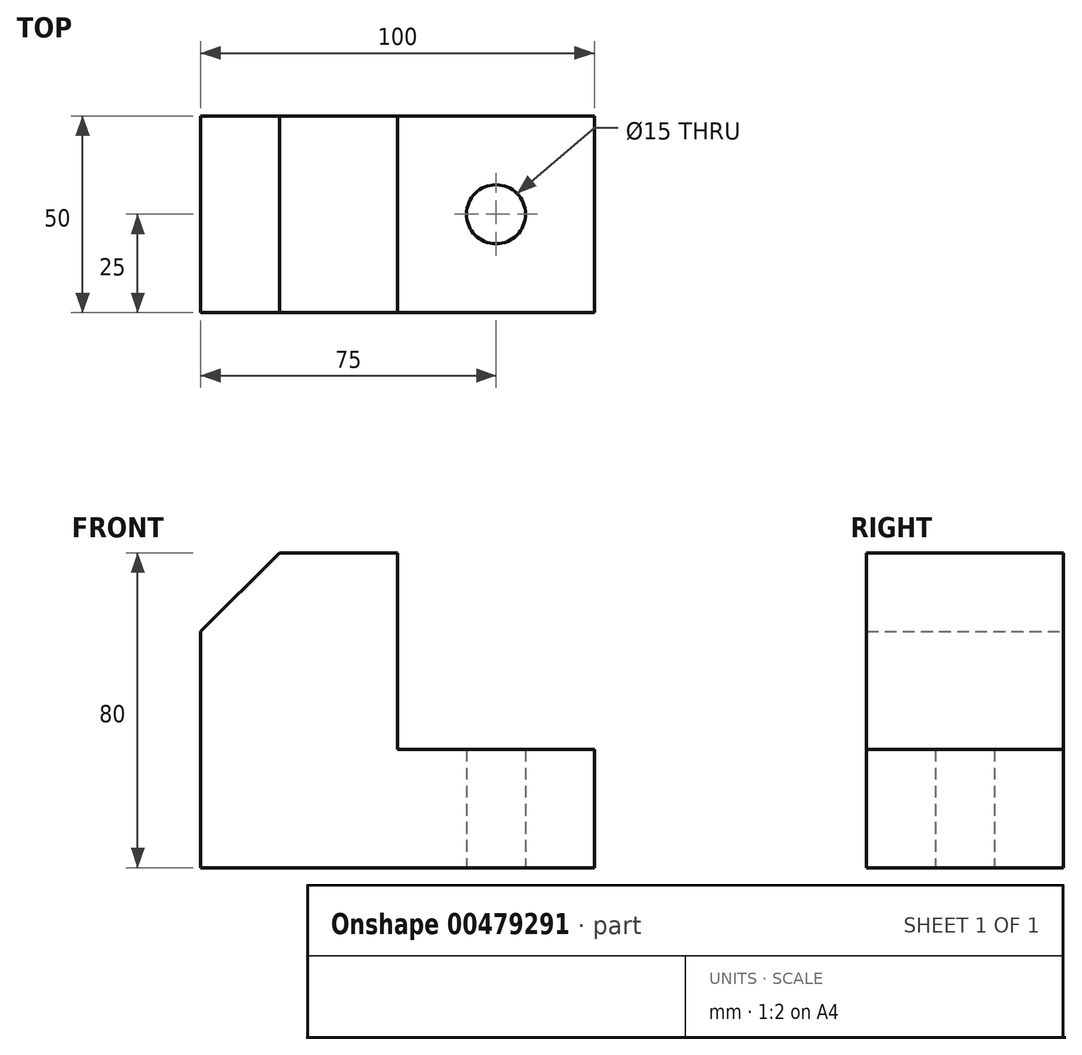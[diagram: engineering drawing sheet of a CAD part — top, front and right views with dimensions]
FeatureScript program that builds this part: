
annotation { "Feature Type Name" : "Feature", "Feature Type Description" : "" }
export const myFeature = defineFeature(function(context is Context, id is Id, definition is map)
    precondition{}
    {
        {
            var Q0;
            Q0=qCreatedBy(makeId("Top.planeOp"),FACE);
            var sketch = newSketch(context, id + "F0", { "sketchPlane" : qUnion([Q0])});
            skLineSegment(sketch, "E0.bottom", {"start": v(0, 0) * mm, "end": v(100, 0) * mm});
            skLineSegment(sketch, "E0.top", {"start": v(0, 50) * mm, "end": v(100, 50) * mm});
            skLineSegment(sketch, "E0.left", {"start": v(0, 0) * mm, "end": v(0, 50) * mm});
            skLineSegment(sketch, "E0.right", {"start": v(100, 0) * mm, "end": v(100, 50) * mm});
            skCircle(sketch, "E1", {"center": v(75, 25) * mm, "radius": 7.5 * mm});
            skSolve(sketch);
        }
        {
            var Q0;
            Q0 = qSketchRegion(id + "F0", true);
            extrude(context, id + "F1", {"entities" : qUnion([Q0]), "depth" : 80 * mm});
        }
        {
            var Q0;
            Q0=makeQuery(id+"F1.opExtrude","SWEPT_FACE",FACE,{"disambiguationData":[OSD([sQuery(id+"F0.wireOp",EDGE,"E0.bottom")])]});
            var sketch = newSketch(context, id + "F2", { "sketchPlane" : qUnion([Q0])});
            skLineSegment(sketch, "E2.bottom", {"start": v(100, 80) * mm, "end": v(50, 80) * mm});
            skLineSegment(sketch, "E2.top", {"start": v(100, 30) * mm, "end": v(50, 30) * mm});
            skLineSegment(sketch, "E2.left", {"start": v(100, 80) * mm, "end": v(100, 30) * mm});
            skLineSegment(sketch, "E2.right", {"start": v(50, 80) * mm, "end": v(50, 30) * mm});
            skSolve(sketch);
        }
        {
            var Q0;
            Q0 = qSketchRegion(id + "F2", true);
            var Q1;
            Q1=makeQuery(id+"F1.opExtrude","SWEPT_FACE",FACE,{"disambiguationData":[OSD([sQuery(id+"F0.wireOp",EDGE,"E0.top")])]});
            extrude(context, id + "F3", {"entities" : qUnion([Q0]), "operationType" : NewBodyOperationType.REMOVE, "endBound" : BoundingType.UP_TO_SURFACE, "oppositeDirection" : true, "endBoundEntityFace" : qUnion([Q1]), "depth" : 25 * mm});
        }
        {
            var Q0;
            Q0=makeQuery(id+"F1.opExtrude","CAP_EDGE",EDGE,{"disambiguationData":[OSD([sQuery(id+"F0.wireOp",EDGE,"E0.left")])],"isStart":false});
            chamfer(context, id + "F4", {"entities" : qUnion([Q0]), "width" : 20 * mm, "tangentPropagation" : true});
        }
    });
